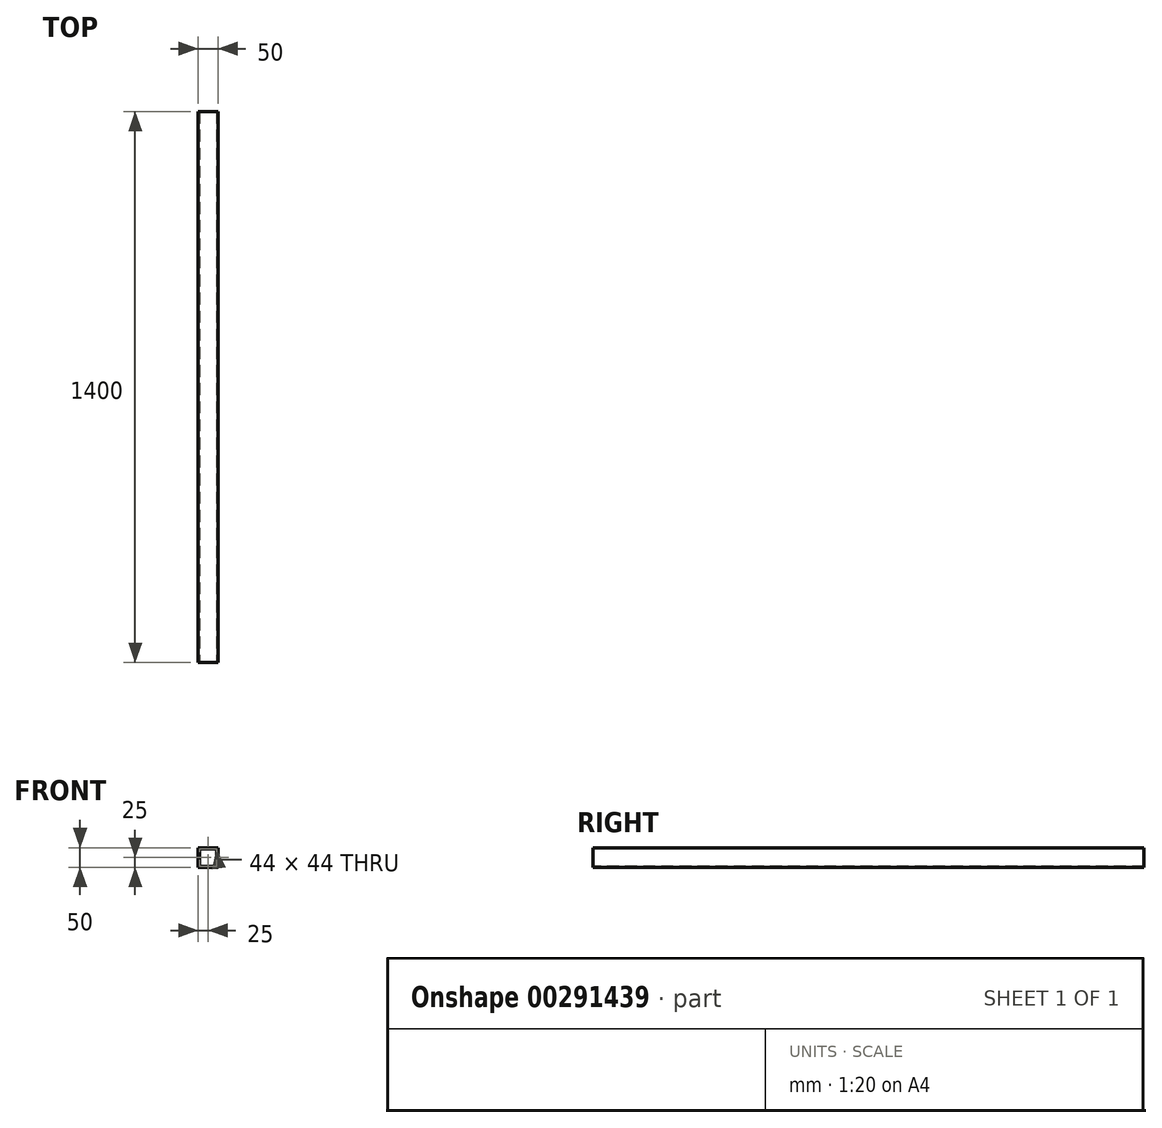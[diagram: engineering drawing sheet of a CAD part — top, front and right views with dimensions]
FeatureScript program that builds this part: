
annotation { "Feature Type Name" : "Feature", "Feature Type Description" : "" }
export const myFeature = defineFeature(function(context is Context, id is Id, definition is map)
    precondition{}
    {
        {
            var Q0;
            Q0=qCreatedBy(makeId("Front.planeOp"),FACE);
            var sketch = newSketch(context, id + "F0", { "sketchPlane" : qUnion([Q0])});
            skLineSegment(sketch, "E0.bottom", {"start": v(25, 25) * mm, "end": v(-25, 25) * mm});
            skLineSegment(sketch, "E0.top", {"start": v(25, -25) * mm, "end": v(-25, -25) * mm});
            skLineSegment(sketch, "E0.left", {"start": v(25, 25) * mm, "end": v(25, -25) * mm});
            skLineSegment(sketch, "E0.right", {"start": v(-25, 25) * mm, "end": v(-25, -25) * mm});
            skPoint(sketch, "E0.middle", {"position": v(0, 0) * mm});
            skLineSegment(sketch, "E1.0", {"start": v(22, 22) * mm, "end": v(-22, 22) * mm});
            skLineSegment(sketch, "E1.1", {"start": v(22, 22) * mm, "end": v(22, -22) * mm});
            skLineSegment(sketch, "E1.2", {"start": v(22, -22) * mm, "end": v(-22, -22) * mm});
            skLineSegment(sketch, "E1.3", {"start": v(-22, 22) * mm, "end": v(-22, -22) * mm});
            skSolve(sketch);
        }
        {
            var Q0;
            Q0 = qSketchRegion(id + "F0", true);
            extrude(context, id + "F1", {"entities" : qUnion([Q0]), "oppositeDirection" : true, "depth" : 1400 * mm});
        }
    });
